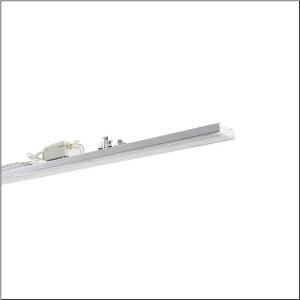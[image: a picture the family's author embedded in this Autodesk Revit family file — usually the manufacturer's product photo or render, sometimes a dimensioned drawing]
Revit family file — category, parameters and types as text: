
# Revit family: licross_r__21_recessed_mo_52tl18dv4e5g_229a
name_source: partatom
category: Lighting Fixtures
units: mm (PartAtom-declared; Revit-internal decimal feet)

## family parameters
Cut with Voids When Loaded = No
Host = Face
Light Source = No
Part Type = Normal
Room Calculation Point = No
Round Connector Dimension = Use Diameter
Shared = No

## types (1)
- --- (1 x LED, 14980 lm, 85.3 W, 4000K)
    Apparent Load = 85 VA
    CIE Flux Codes = 79 95 99 100 100
    Color Rendering = 80
    Color Temperature = 4000K
    Default Elevation = 1800 mm
    Description = Licross® 21 Recessed MO, luminaire insert, of sheet steel, galvanised, coil coated, white, length: 2.250mm, width: 66mm, height: 67mm, LED rated luminous flux: 14.980lm, light colour: 840, control gear: DALI 2, with plug, 5-pole, with phase selection, mains connection: 220..240V, AC, 50/60Hz, rated input power: 85W, halogen-free wiring, primary light control with lens, of plastic, primary optical cover: cover, of PMMA, light emission: direct distribution, primary light characteristic: symmetric, protection rating (complete): IP40, insulation class (complete): insulation class I (protective earthing), certification: CE, ENEC, VDE, UKCA, protection symbol: D if used in an environment without relevant dust loads with corresponding accessories, impact resistance: IK06, permissible ambient temperature for indoor applications: -25..+35°C, corresponds to IFS (International Featured Standards) requirements for safety and quality in the food industry, reducing of maximum allowable ambient temperature of 5°C with ceiling mounting, LABS conformity tested according to VDMA 24364:2018-05, packaging unit: 1 piece
    Height = 58 mm
    Lamp = 1 x LED
    Lamp Light Flux = 14980 lm
    Lamp Power = 85.3 W
    Lamp count = 1
    Length = 2250 mm
    Luminous efficacy = 176 lm/W
    Manufacturer = Siteco
    ModVariant = No
    Model = 52TL18DV4E5G
    Mounting Place = Ceiling
    Mounting Type = Pendant
    Number of Poles = 1
    OnlyDefault = Yes
    Power Factor = 1
    Product Name = Licross® 21 Recessed MO
    Product group = luminaire insert
    ProductGroupID = 901
    Protection Class = Protection class I
    Protection Degree = IP 40
    RLX_Detail_Level = 1
    RLX_Emergency_Light_Flux = 0 lm
    RLX_Emergency_Type = 0
    RLX_Emergency_Type_DB = No
    RlxData = <blob elided: 29641 chars, md5=7ab2ecfc>
    Socket = socket
    Standby Power = 0 W
    System Light Flux = 14980 lm
    System Power = 85 W
    Type Comments = factory setting: luminous flux: 100 % | dim-lin: 254 | 390 mA
    Type Image = l_1296930.jpg
    URL = http://relux.com
    VarID = @adj_057585
    Voltage = 0 V
    Weight = 0.00 kg
    Width = 66 mm

## geometry (parser evidence)
native form markers: Blend x4, Sweep x11
no freeform markers — native parametric forms only
